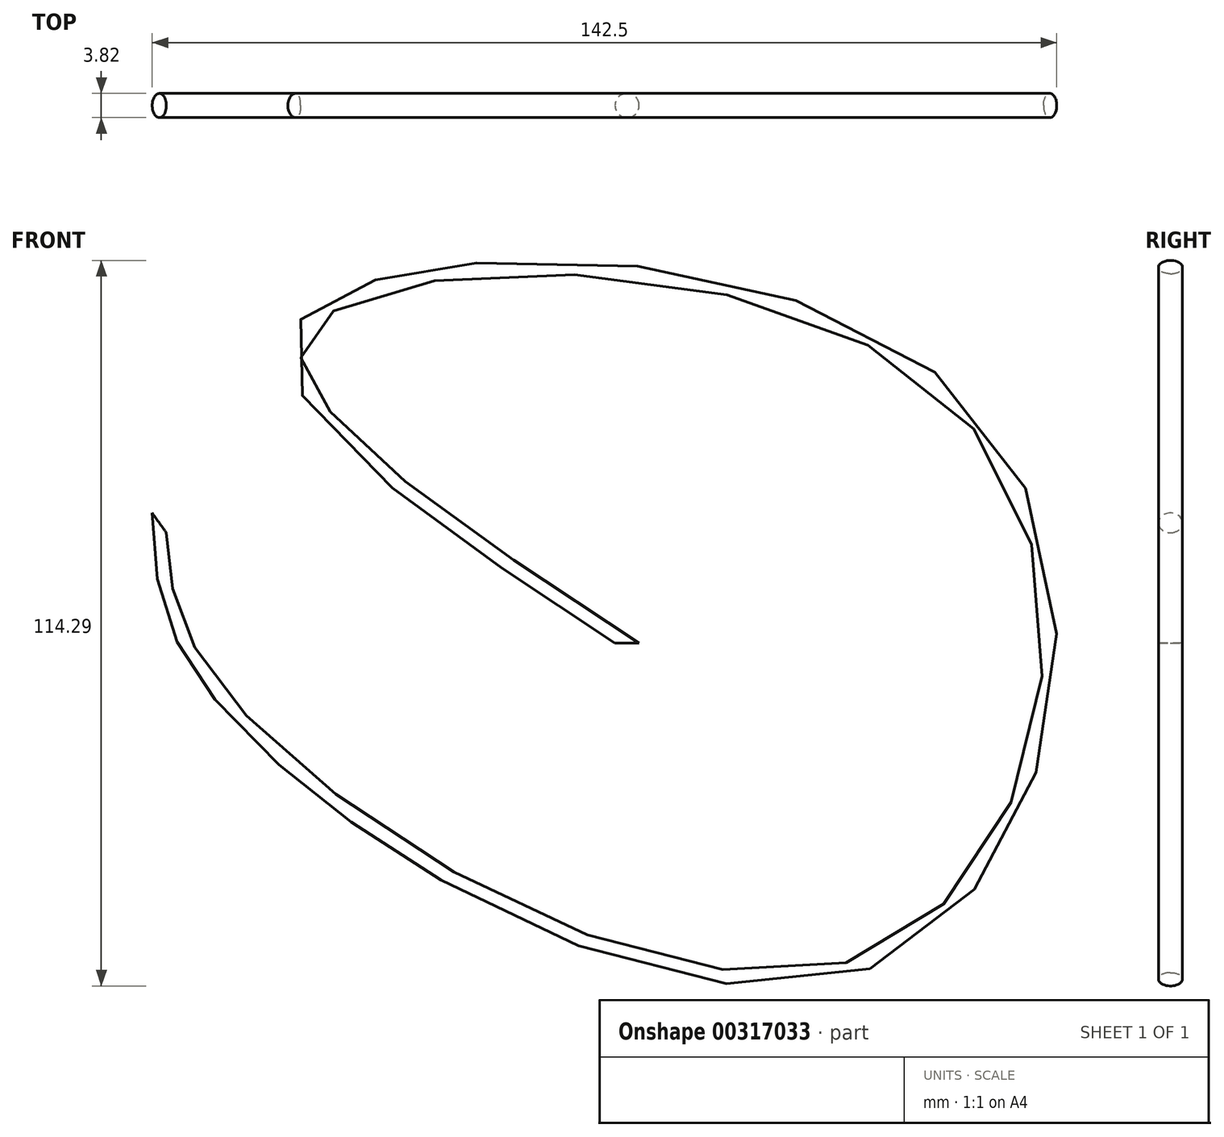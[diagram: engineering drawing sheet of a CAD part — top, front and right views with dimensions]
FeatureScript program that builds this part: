
annotation { "Feature Type Name" : "Feature", "Feature Type Description" : "" }
export const myFeature = defineFeature(function(context is Context, id is Id, definition is map)
    precondition{}
    {
        {
            var Q0;
            Q0=qCreatedBy(makeId("Front.planeOp"),FACE);
            var sketch = newSketch(context, id + "F0", { "sketchPlane" : qUnion([Q0])});
            skFitSpline(sketch, "E0", {"points": [v(0, 0) * mm, v(-50.72, 50) * mm, v(53, 37.16) * mm, v(39.54, -49.58) * mm, v(-63.14, -9.42) * mm, v(-73.7, 18.94) * mm], "startDerivative": vector(-464.98, 304.46) * mm, "endDerivative": vector(-9.07, 203.76) * mm});
            skSolve(sketch);
        }
        {
            var Q0;
            Q0=qCreatedBy(makeId("Top.planeOp"),FACE);
            var sketch = newSketch(context, id + "F1", { "sketchPlane" : qUnion([Q0])});
            skCircle(sketch, "E1", {"center": v(0, 0) * mm, "radius": 1.9 * mm});
            skSolve(sketch);
        }
        {
            var Q0;
            Q0 = qSketchRegion(id + "F1", true);
            var Q1;
            Q1 = qConstructionFilter(qBodyType(qCreatedBy(id + "F0" ,EDGE), BodyType.WIRE), ConstructionObject.NO);
            sweep(context, id + "F2", {"profiles" : qUnion([Q0]), "path" : qUnion([Q1])});
        }
    });
